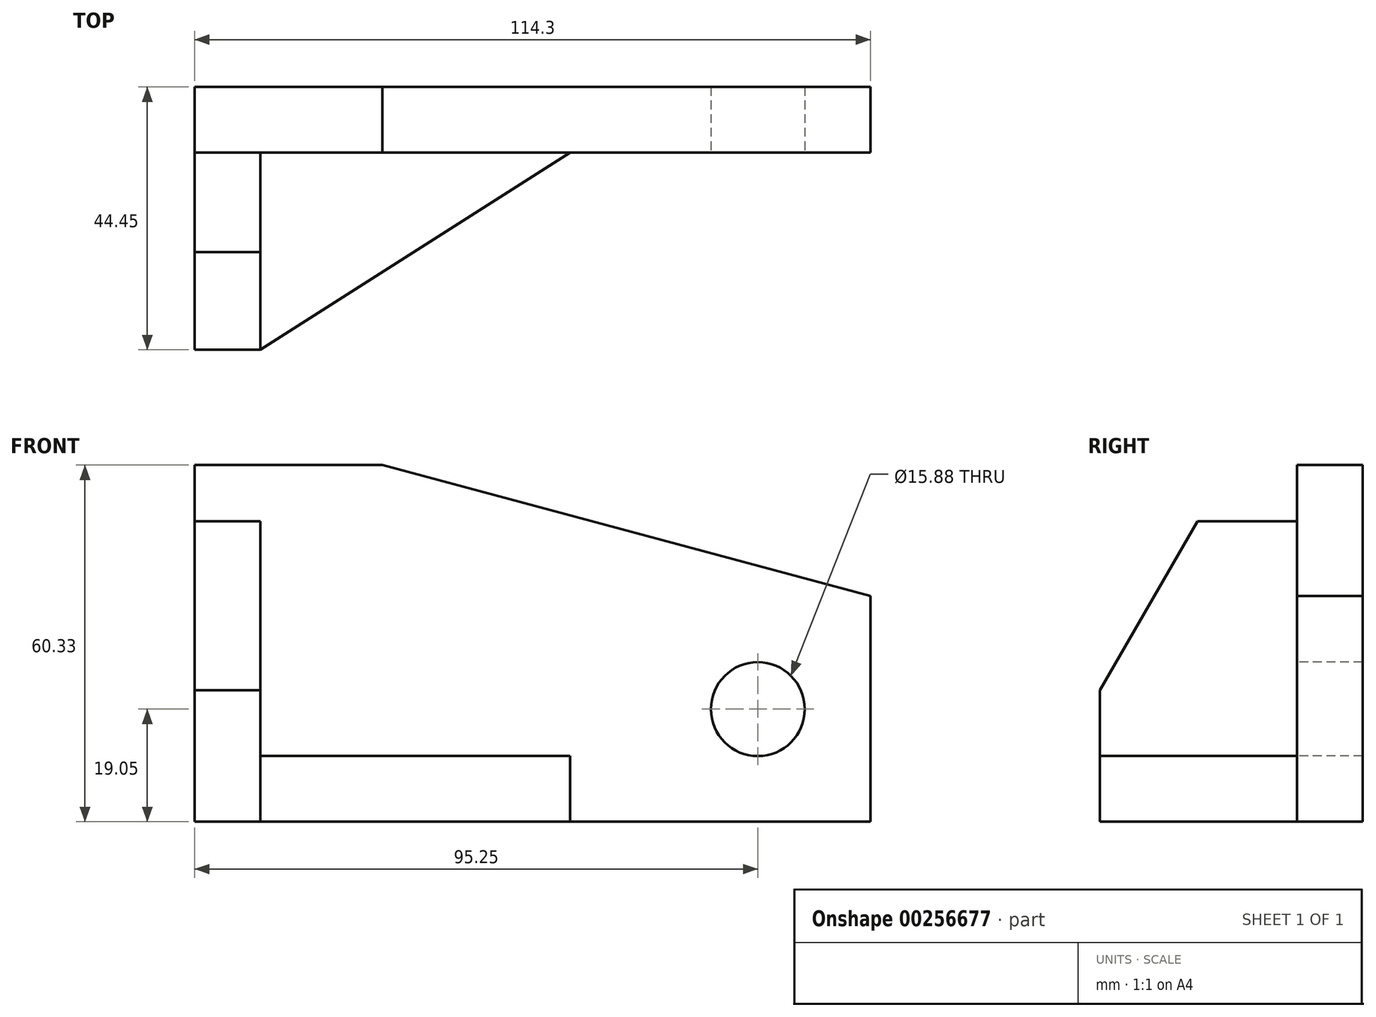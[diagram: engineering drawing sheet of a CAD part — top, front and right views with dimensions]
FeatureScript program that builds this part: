
annotation { "Feature Type Name" : "Feature", "Feature Type Description" : "" }
export const myFeature = defineFeature(function(context is Context, id is Id, definition is map)
    precondition{}
    {
        {
            var Q0;
            Q0=qCreatedBy(makeId("Top.planeOp"),FACE);
            var sketch = newSketch(context, id + "F0", { "sketchPlane" : qUnion([Q0])});
            skLineSegment(sketch, "E0", {"start": v(0, 0) * mm, "end": v(0, 44.45) * mm});
            skLineSegment(sketch, "E1", {"start": v(0, 44.45) * mm, "end": v(114.3, 44.45) * mm});
            skLineSegment(sketch, "E2", {"start": v(0, 0) * mm, "end": v(11.11, 0) * mm});
            skLineSegment(sketch, "E3", {"start": v(114.3, 44.45) * mm, "end": v(114.3, 33.34) * mm});
            skLineSegment(sketch, "E4", {"start": v(114.3, 33.34) * mm, "end": v(0, 33.34) * mm});
            skLineSegment(sketch, "E5", {"start": v(11.11, 0) * mm, "end": v(11.11, 33.34) * mm});
            skLineSegment(sketch, "E6", {"start": v(63.5, 33.34) * mm, "end": v(11.11, 0) * mm});
            skSolve(sketch);
        }
        {
            var Q0;
            {var subQ4=sQuery(id+"F0.wireOp",EDGE,"E5");Q0=makeQuery(id+"F0.imprint","IMPRINT",FACE,{"disambiguationData":[TD([[makeQuery(id+"F0.imprint","IMPRINT",EDGE,{"derivedFrom":subQ4}),1.0]])]});}
            extrude(context, id + "F1", {"entities" : qUnion([Q0]), "depth" : 50.8 * mm});
        }
        {
            var Q0;
            {var subQ3=sQuery(id+"F0.wireOp",EDGE,"E1");Q0=makeQuery(id+"F0.imprint","IMPRINT",FACE,{"disambiguationData":[TD([[makeQuery(id+"F0.imprint","IMPRINT",EDGE,{"derivedFrom":subQ3}),-1.0]])]});}
            extrude(context, id + "F2", {"entities" : qUnion([Q0]), "operationType" : NewBodyOperationType.ADD, "depth" : 60.32 * mm});
        }
        {
            var Q0;
            {var subQ0=sQuery(id+"F0.wireOp",EDGE,"E5");Q0=makeQuery(id+"F0.imprint","IMPRINT",FACE,{"disambiguationData":[TD([[makeQuery(id+"F0.imprint","IMPRINT",EDGE,{"derivedFrom":subQ0}),-1.0]])]});}
            extrude(context, id + "F3", {"entities" : qUnion([Q0]), "operationType" : NewBodyOperationType.ADD, "depth" : 11.1 * mm});
        }
        {
            var Q0;
            Q0=makeQuery(id+"F2.opExtrude","SWEPT_FACE",FACE,{"disambiguationData":[OSD([sQuery(id+"F0.wireOp",EDGE,"E4")])]});
            var sketch = newSketch(context, id + "F4", { "sketchPlane" : qUnion([Q0])});
            skPoint(sketch, "E7", {"position": v(31.75, 60.33) * mm});
            skLineSegment(sketch, "E8", {"start": v(31.75, 60.33) * mm, "end": v(114.3, 38.2) * mm});
            skLineSegment(sketch, "E9", {"start": v(114.3, 0) * mm, "end": v(114.3, 60.33) * mm});
            skLineSegment(sketch, "E10", {"start": v(31.75, 60.33) * mm, "end": v(114.3, 60.33) * mm});
            skLineSegment(sketch, "E11", {"start": v(31.75, 60.33) * mm, "end": v(0, 60.33) * mm});
            skLineSegment(sketch, "E12", {"start": v(0, 60.33) * mm, "end": v(0, 0) * mm});
            skLineSegment(sketch, "E13", {"start": v(0, 0) * mm, "end": v(114.3, 0) * mm});
            skPoint(sketch, "E14", {"position": v(95.25, 0) * mm});
            skPoint(sketch, "E15", {"position": v(95.25, 19.05) * mm});
            skCircle(sketch, "E16", {"center": v(95.25, 19.05) * mm, "radius": 7.94 * mm});
            skSolve(sketch);
        }
        {
            var Q0;
            {var subQ0=sQuery(id+"F4.wireOp",EDGE,"E8");Q0=makeQuery(id+"F4.imprint","IMPRINT",FACE,{"disambiguationData":[TD([[makeQuery(id+"F4.imprint","IMPRINT",EDGE,{"derivedFrom":subQ0}),1.0]])]});}
            extrude(context, id + "F5", {"entities" : qUnion([Q0]), "operationType" : NewBodyOperationType.REMOVE, "oppositeDirection" : true, "depth" : 11.1 * mm});
        }
        {
            var Q0;
            Q0=makeQuery(id+"F4.imprint","IMPRINT",FACE,{"disambiguationData":[TD([[makeQuery(id+"F4.imprint","IMPRINT",EDGE,{"derivedFrom":sQuery(id+"F4.wireOp",EDGE,"E16")}),1.0]])]});
            extrude(context, id + "F6", {"entities" : qUnion([Q0]), "operationType" : NewBodyOperationType.REMOVE, "oppositeDirection" : true, "depth" : 11.1 * mm});
        }
        {
            var Q0;
            {var subQ0=sQuery(id+"F0.wireOp",EDGE,"E0");Q0=makeQuery(id+"F2.boolean.opBoolean","MERGE",FACE,{"derivedFrom":[makeQuery(id+"F1.opExtrude","SWEPT_FACE",FACE,{"disambiguationData":[OSD([subQ0])]}),makeQuery(id+"F2.opExtrude","SWEPT_FACE",FACE,{"disambiguationData":[OSD([subQ0])]})]});}
            var sketch = newSketch(context, id + "F7", { "sketchPlane" : qUnion([Q0])});
            skPoint(sketch, "E17", {"position": v(0, 22.23) * mm});
            skLineSegment(sketch, "E18", {"start": v(0, 22.22) * mm, "end": v(-16.5, 50.8) * mm});
            skLineSegment(sketch, "E19", {"start": v(0, 0) * mm, "end": v(-44.45, 0) * mm});
            skLineSegment(sketch, "E20", {"start": v(-44.45, 0) * mm, "end": v(-44.45, 60.33) * mm});
            skLineSegment(sketch, "E21", {"start": v(-44.45, 60.33) * mm, "end": v(-33.34, 60.33) * mm});
            skLineSegment(sketch, "E22", {"start": v(-33.34, 60.33) * mm, "end": v(-33.34, 50.8) * mm});
            skLineSegment(sketch, "E23", {"start": v(-33.34, 50.8) * mm, "end": v(0, 50.8) * mm});
            skLineSegment(sketch, "E24", {"start": v(0, 50.8) * mm, "end": v(0, 0) * mm});
            skSolve(sketch);
        }
        {
            var Q0;
            {var subQ0=sQuery(id+"F7.wireOp",EDGE,"E18");Q0=makeQuery(id+"F7.imprint","IMPRINT",FACE,{"disambiguationData":[TD([[makeQuery(id+"F7.imprint","IMPRINT",EDGE,{"derivedFrom":subQ0}),-1.0]])]});}
            extrude(context, id + "F8", {"entities" : qUnion([Q0]), "operationType" : NewBodyOperationType.REMOVE, "oppositeDirection" : true, "depth" : 11.1 * mm});
        }
    });
